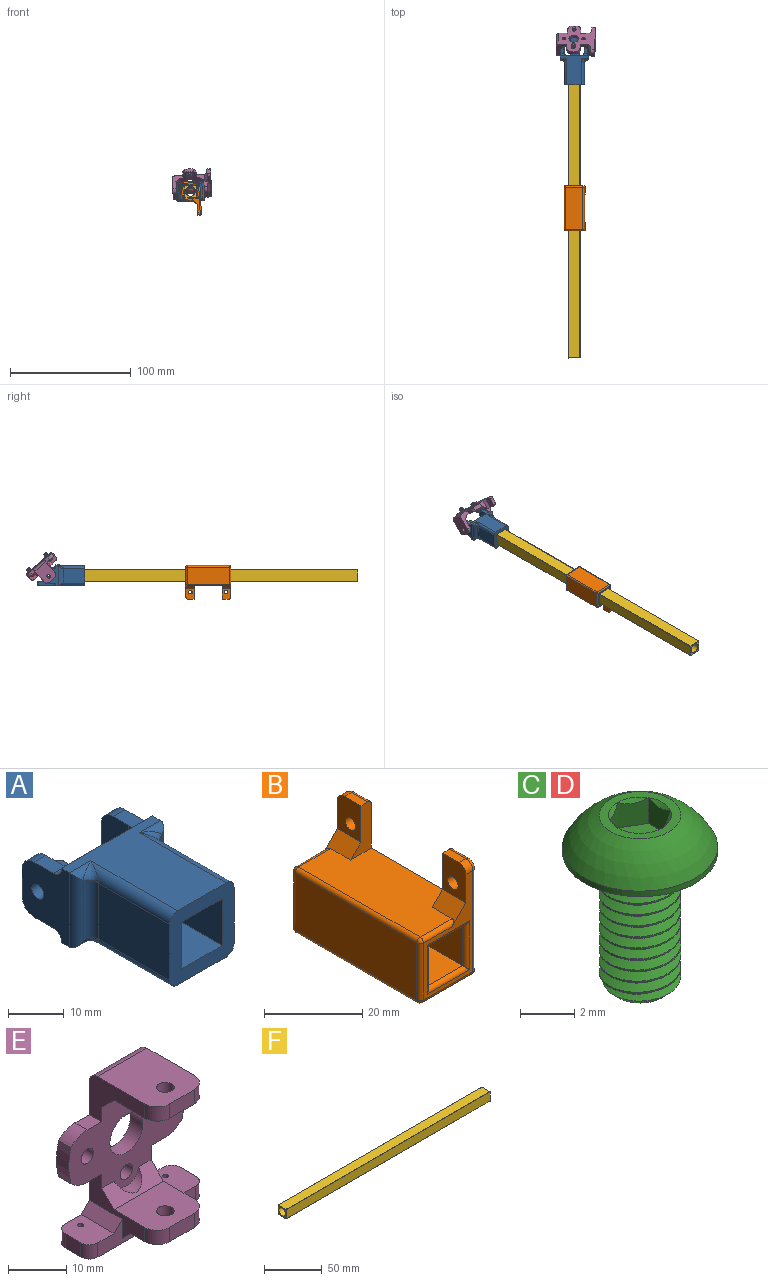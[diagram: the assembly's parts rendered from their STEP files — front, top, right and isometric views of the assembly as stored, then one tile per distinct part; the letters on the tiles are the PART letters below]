
ASSEMBLY  parts=6 mates=5
PART A: 69 faces, bbox 23.1x39.6x16.9 mm
  f0: plane 39.6x23.11mm, normal (0,0,-1), area 411.9mm2, adj f2,f3,f12,f13,f14,f15,f16,f19
  f1: plane 23x13.18mm, normal (0,1,0), area 44.4mm2, adj f10,f13,f14,f49,f50,f51,f54,f55
  f2: plane 6x0.13mm, normal (0,1,0), area 0.8mm2, adj f0,f14,f52,f65
  f3: plane 6x0.13mm, normal (0,1,0), area 0.8mm2, adj f0,f13,f53,f64
  f4: plane 10.25x10.25mm, normal (0,-1,0), area 3.1mm2, adj f5,f6,f7,f11,f55,f56,f57,f58
  f5: plane 20x10.25mm, normal (0,0,-1), area 205mm2, adj f4,f6,f11,f12
  f6: plane 20x10.25mm, normal (-1,0,0), area 205mm2, adj f4,f5,f7,f12
  f7: plane 20x10.25mm, normal (0,0,1), area 205mm2, adj f4,f6,f11,f12
  f8: plane 18.05x12.25mm, normal (-1,0,0), area 221.1mm2, adj f12,f15,f18,f32
  f9: plane 18.05x12.25mm, normal (1,0,0), area 221.1mm2, adj f12,f16,f17,f27
  f10: plane 24x23mm, normal (0,0,1), area 315.5mm2, adj f1,f12,f13,f14,f17,f18,f21,f22
  f11: plane 20x10.25mm, normal (1,0,0), area 205mm2, adj f4,f5,f7,f12
  f12: plane 16.25x16.25mm, normal (0,-1,0), area 155.6mm2, adj f0,f5,f6,f7,f8,f9,f10,f11
  f13: plane 16.25x12mm, normal (-1,0,0), area 143.3mm2, adj f0,f1,f3,f10,f23,f35,f36,f37
  f14: plane 16.25x12mm, normal (1,0,0), area 143.3mm2, adj f0,f1,f2,f10,f20,f42,f43,f44
  f15: cylinder r=2mm len=22mm, axis (0,1,0), area 61.1mm2, adj f0,f8,f12,f33,f34
  f16: cylinder r=2mm len=22mm, axis (0,-1,0), area 61.1mm2, adj f0,f9,f12,f28,f29
  f17: cylinder r=2mm len=22mm, axis (0,1,0), area 61.1mm2, adj f9,f10,f12,f25,f26
  f18: cylinder r=2mm len=22mm, axis (0,-1,0), area 61.1mm2, adj f8,f10,f12,f30,f31
  f19: cylinder r=2mm len=5.38mm, axis (-1,0,0), area 7.1mm2, adj f0,f20,f29
  f20: cylinder r=2mm len=16.25mm, axis (0,0,-1), area 42.6mm2, adj f14,f19,f21,f25,f26,f27,f28,f29
  f21: cylinder r=2mm len=5.38mm, axis (1,0,0), area 7.1mm2, adj f10,f20,f25
  f22: cylinder r=2mm len=5.38mm, axis (1,0,0), area 7.1mm2, adj f10,f23,f30
  f23: cylinder r=2mm len=16.25mm, axis (0,0,1), area 42.6mm2, adj f13,f22,f24,f30,f31,f32,f33,f34
  f24: cylinder r=2mm len=5.38mm, axis (-1,0,0), area 7.1mm2, adj f0,f23,f34
  f25: bspline ~3.99x3.99mm, area 6.7mm2, adj f17,f20,f21,f26
  f26: bspline ~1.99x1.74mm, area 0.9mm2, adj f17,f20,f25,f27
  f27: cylinder r=2mm len=12.25mm, axis (0,0,-1), area 34.6mm2, adj f9,f20,f26,f28
  f28: bspline ~1.99x1.74mm, area 0.9mm2, adj f16,f20,f27,f29
  f29: bspline ~3.99x3.99mm, area 6.7mm2, adj f16,f19,f20,f28
  f30: bspline ~3.99x3.99mm, area 6.7mm2, adj f18,f22,f23,f31
  f31: bspline ~1.99x1.74mm, area 0.9mm2, adj f18,f23,f30,f32
  f32: cylinder r=2mm len=12.25mm, axis (0,0,1), area 34.6mm2, adj f8,f23,f31,f33
  f33: bspline ~1.99x1.74mm, area 0.9mm2, adj f15,f23,f32,f34
  f34: bspline ~3.99x3.99mm, area 6.7mm2, adj f15,f23,f24,f33
  f35: plane 5x3.17mm, normal (0,0,-1), area 15.1mm2, adj f13,f40,f41,f50,f53
  f36: plane 5x3.17mm, normal (0,0,1), area 15.1mm2, adj f13,f37,f41,f50,f54
  f37: cylinder r=3mm len=3mm, axis (-1,0,0), area 14.1mm2, adj f13,f36,f38,f41
  f38: plane 6x3mm, normal (0,1,0), area 18mm2, adj f13,f37,f40,f41
  f39: cylinder r=1.5mm len=3mm, axis (-1,0,0), area 28.3mm2, adj f13,f41
  f40: cylinder r=3mm len=3mm, axis (-1,0,0), area 14.1mm2, adj f13,f35,f38,f41
  f41: plane 12x7mm, normal (1,0,0), area 73.1mm2, adj f35,f36,f37,f38,f39,f40,f50
  f42: plane 5x3.17mm, normal (0,0,-1), area 15.1mm2, adj f14,f47,f48,f49,f52
  f43: plane 5x3.17mm, normal (0,0,1), area 15.1mm2, adj f14,f44,f48,f49,f51
  f44: cylinder r=3mm len=3mm, axis (1,0,0), area 14.1mm2, adj f14,f43,f45,f48
  f45: plane 6x3mm, normal (0,1,0), area 18mm2, adj f14,f44,f47,f48
  f46: cylinder r=1.5mm len=3mm, axis (1,0,0), area 28.3mm2, adj f14,f48
  f47: cylinder r=3mm len=3mm, axis (1,0,0), area 14.1mm2, adj f14,f42,f45,f48
  f48: plane 12x7mm, normal (-1,0,0), area 73.1mm2, adj f42,f43,f44,f45,f46,f47,f49
  f49: cylinder r=3mm len=16mm, axis (0,0,1), area 63.9mm2, adj f1,f42,f43,f48,f51,f52,f65
  f50: cylinder r=3mm len=16mm, axis (0,0,1), area 63.9mm2, adj f1,f35,f36,f41,f53,f54,f64
  f51: cylinder r=2mm len=6mm, axis (-1,0,0), area 14.4mm2, adj f1,f14,f43,f49
  f52: cylinder r=2mm len=6mm, axis (1,0,0), area 14.4mm2, adj f2,f14,f42,f49
  f53: cylinder r=2mm len=6mm, axis (-1,0,0), area 14.4mm2, adj f3,f13,f35,f50
  f54: cylinder r=2mm len=6mm, axis (1,0,0), area 14.4mm2, adj f1,f13,f36,f50
  f55: plane 19.5x11mm, normal (0,0,1), area 150.2mm2, adj f1,f4,f56,f57,f59,f60,f61,f62
  f56: plane 10.1x4mm, normal (-1,0,0), area 40.4mm2, adj f1,f4,f55,f58
  f57: plane 10.1x4mm, normal (1,0,0), area 40.4mm2, adj f1,f4,f55,f58
  f58: plane 10.1x4mm, normal (0,0,-1), area 40.4mm2, adj f1,f4,f56,f57
  f59: plane 12.5x3.08mm, normal (1,0,0), area 38.4mm2, adj f0,f55,f63,f65
  f60: plane 12.5x3.08mm, normal (-1,0,0), area 38.4mm2, adj f0,f55,f62,f64
  f61: plane 5x2.51mm, normal (0,1,0), area 7.8mm2, adj f55,f62,f63,f67
  f62: cylinder r=1mm len=3.08mm, axis (0,0,-1), area 4.8mm2, adj f0,f55,f60,f61,f67
  f63: cylinder r=1mm len=3.08mm, axis (0,0,1), area 4.8mm2, adj f0,f55,f59,f61,f67
  f64: cylinder r=2mm len=3.08mm, axis (0,0,1), area 9.7mm2, adj f0,f3,f50,f55,f60
  f65: cylinder r=2mm len=3.08mm, axis (0,0,-1), area 9.7mm2, adj f0,f2,f49,f55,f59
  f66: cylinder r=1.99mm len=3.35mm, axis (0,1,0), area 8mm2, adj f0,f67,f68
  f67: torus R=2.99mm, axis (0,1,0), area 8.1mm2, adj f0,f61,f62,f63,f66
  f68: torus R=0.99mm, axis (0,1,0), area 4.2mm2, adj f0,f66
PART B: 51 faces, bbox 16.2x37.3x28.4 mm
  f0: plane 35x26.2mm, normal (1,0,0), area 643.9mm2, adj f2,f5,f6,f17,f18,f22,f31,f32
  f1: plane 25.2x14.2mm, normal (0,-1,0), area 82.8mm2, adj f4,f19,f24,f34,f36,f38,f40,f47
  f2: plane 12x6mm, normal (0,1,0), area 40.3mm2, adj f0,f3,f4,f5,f24,f42
  f3: plane 4.75x2mm, normal (0,0,1), area 9.5mm2, adj f2,f4,f19,f42
  f4: plane 9x6.75mm, normal (-1,0,0), area 52.8mm2, adj f1,f2,f3,f18,f19,f24
  f5: plane 35x15.2mm, normal (0,0,1), area 463mm2, adj f0,f2,f6,f16,f23,f24,f25,f34
  f6: plane 12x6mm, normal (0,-1,0), area 40.3mm2, adj f0,f5,f8,f9,f16,f33
  f7: plane 25.2x14.2mm, normal (0,1,0), area 82.8mm2, adj f9,f16,f20,f25,f27,f29,f31,f43
  f8: plane 4.75x2mm, normal (0,0,1), area 9.5mm2, adj f6,f9,f20,f33
  f9: plane 9x6.75mm, normal (-1,0,0), area 52.8mm2, adj f6,f7,f8,f16,f17,f20
  f10: plane 35x10.2mm, normal (0,0,-1), area 357mm2, adj f11,f15,f43,f47
  f11: plane 35x10.2mm, normal (-1,0,0), area 357mm2, adj f10,f12,f44,f48
  f12: plane 35x10.2mm, normal (0,0,1), area 357mm2, adj f11,f15,f46,f50
  f13: plane 35x14.2mm, normal (-1,0,0), area 497mm2, adj f21,f23,f27,f36
  f14: plane 35x14.2mm, normal (0,0,-1), area 497mm2, adj f21,f22,f29,f38
  f15: plane 35x10.2mm, normal (1,0,0), area 357mm2, adj f10,f12,f45,f49
  f16: plane 6.75x4mm, normal (-0.71,0,0.71), area 28.9mm2, adj f5,f6,f7,f9,f25
  f17: cylinder r=1.5mm len=3mm, axis (1,0,0), area 28.3mm2, adj f0,f9
  f18: cylinder r=1.5mm len=3mm, axis (1,0,0), area 28.3mm2, adj f0,f4
  f19: cylinder r=2mm len=2mm, axis (1,0,0), area 6.3mm2, adj f1,f3,f4,f41
  f20: cylinder r=2mm len=2mm, axis (1,0,0), area 6.3mm2, adj f7,f8,f9,f32
  f21: cylinder r=1mm len=35mm, axis (0,1,0), area 55mm2, adj f13,f14,f28,f37
  f22: cylinder r=1mm len=35mm, axis (0,1,0), area 55mm2, adj f0,f14,f30,f39
  f23: cylinder r=1mm len=35mm, axis (0,-1,0), area 55mm2, adj f5,f13,f26,f35
  f24: plane 6.75x4mm, normal (-0.71,0,0.71), area 28.9mm2, adj f1,f2,f4,f5,f34
  f25: cylinder r=1mm len=9.2mm, axis (1,0,0), area 13.9mm2, adj f5,f7,f16,f26
  f26: sphere r=1mm, area 1.6mm2, adj f23,f25,f27
  f27: cylinder r=1mm len=14.2mm, axis (0,0,1), area 22.3mm2, adj f7,f13,f26,f28
  f28: sphere r=1mm, area 1.6mm2, adj f21,f27,f29
  f29: cylinder r=1mm len=14.2mm, axis (-1,0,0), area 22.3mm2, adj f7,f14,f28,f30
  f30: sphere r=1mm, area 1.6mm2, adj f22,f29,f31
  f31: cylinder r=1mm len=25.2mm, axis (0,0,1), area 39.6mm2, adj f0,f7,f30,f32
  f32: torus R=1mm, axis (1,0,0), area 4mm2, adj f0,f20,f31,f33
  f33: cylinder r=1mm len=4.75mm, axis (0,-1,0), area 7.5mm2, adj f0,f6,f8,f32
  f34: cylinder r=1mm len=9.2mm, axis (-1,0,0), area 13.9mm2, adj f1,f5,f24,f35
  f35: sphere r=1mm, area 1.6mm2, adj f23,f34,f36
  f36: cylinder r=1mm len=14.2mm, axis (0,0,-1), area 22.3mm2, adj f1,f13,f35,f37
  f37: sphere r=1mm, area 1.6mm2, adj f21,f36,f38
  f38: cylinder r=1mm len=14.2mm, axis (1,0,0), area 22.3mm2, adj f1,f14,f37,f39
  f39: sphere r=1mm, area 1.6mm2, adj f22,f38,f40
  f40: cylinder r=1mm len=25.2mm, axis (0,0,-1), area 39.6mm2, adj f0,f1,f39,f41
  f41: torus R=1mm, axis (1,0,0), area 4mm2, adj f0,f19,f40,f42
  f42: cylinder r=1mm len=4.75mm, axis (0,-1,0), area 7.5mm2, adj f0,f2,f3,f41
  f43: cylinder r=1mm len=12.2mm, axis (-1,0,0), area 17.2mm2, adj f7,f10,f44,f45
  f44: cylinder r=1mm len=12.2mm, axis (0,0,1), area 17.2mm2, adj f7,f11,f43,f46
  f45: cylinder r=1mm len=12.2mm, axis (0,0,-1), area 17.2mm2, adj f7,f15,f43,f46
  f46: cylinder r=1mm len=12.2mm, axis (1,0,0), area 17.2mm2, adj f7,f12,f44,f45
  f47: cylinder r=1mm len=12.2mm, axis (1,0,0), area 17.2mm2, adj f1,f10,f48,f49
  f48: cylinder r=1mm len=12.2mm, axis (0,0,-1), area 17.2mm2, adj f1,f11,f47,f50
  f49: cylinder r=1mm len=12.2mm, axis (0,0,1), area 17.2mm2, adj f1,f15,f47,f50
  f50: cylinder r=1mm len=12.2mm, axis (-1,0,0), area 17.2mm2, adj f1,f12,f48,f49
PART C: 24 faces, bbox 6.1x6.1x8.3 mm
  f0: cylinder r=1.5mm len=5.63mm, axis (0,0,-1), area 3.8mm2, adj f2,f4,f6,f9
  f1: cone r=1.12mm half-angle=45deg, axis (0,0,1), area 1.9mm2, adj f2,f3,f4,f5
  f2: cone r=1.12mm half-angle=45deg, axis (0,0,1), area 0.5mm2, adj f0,f1,f4,f6
  f3: plane 2.25x2.25mm, normal (0,0,-1), area 4mm2, adj f1
  f4: bspline ~6.44x3.46mm, area 36.5mm2, adj f0,f1,f2,f5,f9
  f5: bspline ~6.15x2.71mm, area 5.5mm2, adj f1,f4,f6,f9
  f6: bspline ~6.27x3.46mm, area 36.4mm2, adj f0,f2,f5,f9
  f7: sphere r=3.17mm, area 28mm2, adj f8,f10
  f8: plane 3x3mm, normal (0,0,1), area 2.9mm2, adj f7,f11,f12,f13,f14,f15,f16
  f9: plane 5.9x5.9mm, normal (0,0,-1), area 19.9mm2, adj f0,f4,f5,f6,f10
  f10: cylinder r=2.85mm len=5.7mm, axis (0,0,1), area 4.4mm2, adj f7,f9
  f11: cone r=1.15mm half-angle=45deg, axis (0,0,1), area 0mm2, adj f8,f18
  f12: cone r=1.15mm half-angle=45deg, axis (0,0,1), area 0mm2, adj f8,f19
  f13: cone r=1.15mm half-angle=45deg, axis (0,0,1), area 0mm2, adj f8,f20
  f14: cone r=1.15mm half-angle=45deg, axis (0,0,1), area 0mm2, adj f8,f21
  f15: cone r=1.15mm half-angle=45deg, axis (0,0,1), area 0mm2, adj f8,f22
  f16: cone r=1.15mm half-angle=45deg, axis (0,0,1), area 0mm2, adj f8,f23
  f17: plane 2.31x2mm, normal (0,0,1), area 3.5mm2, adj f18,f19,f20,f21,f22,f23
  f18: plane 1.59x1.59mm, normal (-1,0,0), area 1.2mm2, adj f11,f17,f19,f23
  f19: plane 1.59x1.44mm, normal (-0.5,-0.87,0), area 1.2mm2, adj f12,f17,f18,f20
  f20: plane 1.59x1.44mm, normal (0.5,-0.87,0), area 1.2mm2, adj f13,f17,f19,f21
  f21: plane 1.59x1.59mm, normal (1,0,0), area 1.2mm2, adj f14,f17,f20,f22
  f22: plane 1.59x1.44mm, normal (0.5,0.87,0), area 1.2mm2, adj f15,f17,f21,f23
  f23: plane 1.59x1.44mm, normal (-0.5,0.87,0), area 1.2mm2, adj f16,f17,f18,f22
PART D: same geometry as C
PART E: 53 faces, bbox 28x16.5x32 mm
  f0: plane 12x6.5mm, normal (0,0,-1), area 67.1mm2, adj f21,f22,f24,f25,f26,f27,f52
  f1: cylinder r=1.5mm len=3mm, axis (0,1,0), area 28.3mm2, adj f4,f5
  f2: cylinder r=1.5mm len=3mm, axis (0,1,0), area 28.3mm2, adj f4,f5
  f3: plane 12x3mm, normal (0,-0.71,-0.71), area 35.1mm2, adj f4,f19,f20,f33,f36
  f4: plane 28x22mm, normal (0,-1,0), area 309.2mm2, adj f1,f2,f3,f6,f7,f8,f9,f10
  f5: plane 30x28mm, normal (0,1,0), area 482.3mm2, adj f1,f2,f6,f7,f8,f9,f10,f11
  f6: plane 3.5x3mm, normal (0,0,-1), area 10.5mm2, adj f4,f5,f10,f22
  f7: plane 3.5x3mm, normal (0,0,1), area 10.5mm2, adj f4,f5,f8,f19
  f8: cylinder r=5.5mm len=3.97mm, axis (0,1,0), area 13.3mm2, adj f4,f5,f7,f9
  f9: cylinder r=14mm len=7.61mm, axis (0,1,0), area 23.1mm2, adj f4,f5,f8,f10
  f10: cylinder r=5.5mm len=3.97mm, axis (0,1,0), area 13.3mm2, adj f4,f5,f6,f9
  f11: plane 3.5x3mm, normal (0,0,-1), area 10.5mm2, adj f4,f5,f12,f21
  f12: cylinder r=5.5mm len=3.97mm, axis (0,1,0), area 13.3mm2, adj f4,f5,f11,f13
  f13: cylinder r=14mm len=7.61mm, axis (0,1,0), area 23.1mm2, adj f4,f5,f12,f14
  f14: cylinder r=5.5mm len=3.97mm, axis (0,1,0), area 13.3mm2, adj f4,f5,f13,f16
  f15: cylinder r=1.5mm len=3mm, axis (0,1,0), area 28.3mm2, adj f4,f5
  f16: plane 3.5x3mm, normal (0,0,1), area 10.5mm2, adj f4,f5,f14,f20
  f17: cylinder r=1.5mm len=3mm, axis (0,1,0), area 28.3mm2, adj f4,f5
  f18: plane 14.5x12mm, normal (0,0,1), area 163.1mm2, adj f19,f20,f29,f30,f31,f32,f34
  f19: plane 13.5x9mm, normal (-1,0,0), area 62.1mm2, adj f3,f4,f5,f7,f18,f31,f33,f34
  f20: plane 13.5x9mm, normal (1,0,0), area 62.1mm2, adj f3,f4,f5,f16,f18,f29,f33,f34
  f21: plane 13.5x11mm, normal (1,0,0), area 49mm2, adj f0,f4,f5,f11,f24,f28,f35,f40
  f22: plane 13.5x11mm, normal (-1,0,0), area 49mm2, adj f0,f4,f5,f6,f26,f28,f35,f40
  f23: cylinder r=4mm len=8mm, axis (0,1,0), area 75.4mm2, adj f4,f5
  f24: cylinder r=3mm len=3mm, axis (0,0,-1), area 14.1mm2, adj f0,f21,f25,f28
  f25: plane 6x3mm, normal (0,-1,0), area 18mm2, adj f0,f24,f26,f28
  f26: cylinder r=3mm len=3mm, axis (0,0,-1), area 14.1mm2, adj f0,f22,f25,f28
  f27: cylinder r=1.5mm len=3mm, axis (0,0,-1), area 28.3mm2, adj f0,f28
  f28: plane 12x10.5mm, normal (0,0,1), area 115.1mm2, adj f21,f22,f24,f25,f26,f27,f35
  f29: cylinder r=3mm len=3mm, axis (0,0,1), area 14.1mm2, adj f18,f20,f30,f33
  f30: plane 6x3mm, normal (0,-1,0), area 18mm2, adj f18,f29,f31,f33
  f31: cylinder r=3mm len=3mm, axis (0,0,1), area 14.1mm2, adj f18,f19,f30,f33
  f32: cylinder r=1.5mm len=3mm, axis (0,0,1), area 28.3mm2, adj f18,f33
  f33: plane 12x10.5mm, normal (0,0,-1), area 115.1mm2, adj f3,f19,f20,f29,f30,f31,f32
  f34: cylinder r=2mm len=12mm, axis (1,0,0), area 37.7mm2, adj f5,f18,f19,f20
  f35: plane 12x3mm, normal (0,-0.71,0.71), area 35.1mm2, adj f4,f21,f22,f28,f37
  f36: cylinder r=3mm len=5.92mm, axis (0,1,0), area 13.5mm2, adj f3,f4
  f37: cylinder r=3mm len=5.92mm, axis (0,1,0), area 13.5mm2, adj f4,f35
  f38: plane 8x6mm, normal (0,0,1), area 45.3mm2, adj f5,f39,f40,f44,f45,f46,f51
  f39: cylinder r=2.1mm len=3mm, axis (0,0,1), area 9.9mm2, adj f38,f40,f46,f48
  f40: plane 23.8x5mm, normal (0,-1,0), area 51.4mm2, adj f21,f22,f38,f39,f41,f48,f49,f50
  f41: cylinder r=2.1mm len=3mm, axis (0,0,1), area 9.9mm2, adj f40,f42,f48,f49
  f42: plane 3.8x3mm, normal (-1,0,0), area 11.4mm2, adj f41,f43,f48,f49
  f43: cylinder r=2.1mm len=3mm, axis (0,0,1), area 9.9mm2, adj f5,f42,f48,f49
  f44: cylinder r=2.1mm len=3mm, axis (0,0,1), area 9.9mm2, adj f5,f38,f46,f48
  f45: cylinder r=0.5mm len=3mm, axis (0,0,1), area 9.4mm2, adj f38,f48
  f46: plane 3.8x3mm, normal (1,0,0), area 11.4mm2, adj f38,f39,f44,f48
  f47: cylinder r=0.5mm len=3mm, axis (0,0,1), area 9.4mm2, adj f48,f49
  f48: plane 28x8mm, normal (0,0,-1), area 218.6mm2, adj f5,f39,f40,f41,f42,f43,f44,f45
  f49: plane 8x6mm, normal (0,0,1), area 45.3mm2, adj f5,f40,f41,f42,f43,f47,f50
  f50: plane 8x2mm, normal (-0.71,0,0.71), area 22.6mm2, adj f5,f22,f40,f49
  f51: plane 8x2mm, normal (0.71,0,0.71), area 22.6mm2, adj f5,f21,f38,f40
  f52: plane 12x2mm, normal (0,-0.71,-0.71), area 33.9mm2, adj f0,f21,f22,f40
PART F: 11 faces, bbox 250x10x10 mm
  f0: plane 250x9.6mm, normal (0,1,0), area 2400mm2, adj f5,f6,f7,f10
  f1: plane 250x9.6mm, normal (0,0,1), area 2400mm2, adj f5,f6,f7,f8
  f2: plane 250x9.6mm, normal (0,-1,0), area 2400mm2, adj f5,f6,f8,f9
  f3: cylinder r=4mm len=250mm, axis (-1,0,0), area 6283.2mm2, adj f5,f6
  f4: plane 250x9.6mm, normal (0,0,-1), area 2400mm2, adj f5,f6,f9,f10
  f5: plane 10x10mm, normal (1,0,0), area 49.7mm2, adj f0,f1,f2,f3,f4,f7,f8,f9
  f6: plane 10x10mm, normal (-1,0,0), area 49.7mm2, adj f0,f1,f2,f3,f4,f7,f8,f9
  f7: cylinder r=0.2mm len=250mm, axis (-1,0,0), area 78.5mm2, adj f0,f1,f5,f6
  f8: cylinder r=0.2mm len=250mm, axis (1,0,0), area 78.5mm2, adj f1,f2,f5,f6
  f9: cylinder r=0.2mm len=250mm, axis (-1,0,0), area 78.5mm2, adj f2,f4,f5,f6
  f10: cylinder r=0.2mm len=250mm, axis (1,0,0), area 78.5mm2, adj f0,f4,f5,f6
PLACE A rot(axis=(0,-1,0),3deg) t=(12.25,-22.84,11.7)mm fixed
PLACE B rot(axis=(1,0,0.03),180deg) t=(12.26,-163.42,11.6)mm
PLACE C rot(axis=(1,-0.01,0.03),139.2deg) t=(11.61,-14.74,24.02)mm
PLACE D rot(axis=(1,-0.01,0.03),139.2deg) t=(12.27,-0.52,11.44)mm
PLACE E rot(axis=(0.39,-0.85,-0.37),102.5deg) t=(11.76,-4.67,21.15)mm
PLACE F rot(axis=(0.03,-0.03,-1),90deg) t=(12.25,-18.84,11.7)mm fixed
MATE fastened C.f10 <-> E.f12  axis (0.04,-0.65,-0.76) through (11.55,-13.83,25.08)mm
MATE revolute A.f39 <-> E.f32  axis (-1,0,-0.05) through (0.77,-12.84,11.1)mm
MATE slider F.f3 <-> B.f1  axis (0,1,0) through (12.25,-268.84,11.7)mm
MATE fastened E.f8 <-> D.f10  axis (0.04,-0.65,-0.76) through (12.2,0.56,12.69)mm
MATE fastened A.f1 <-> F.f3  axis (0,1,0) through (12.25,-18.84,11.7)mm
